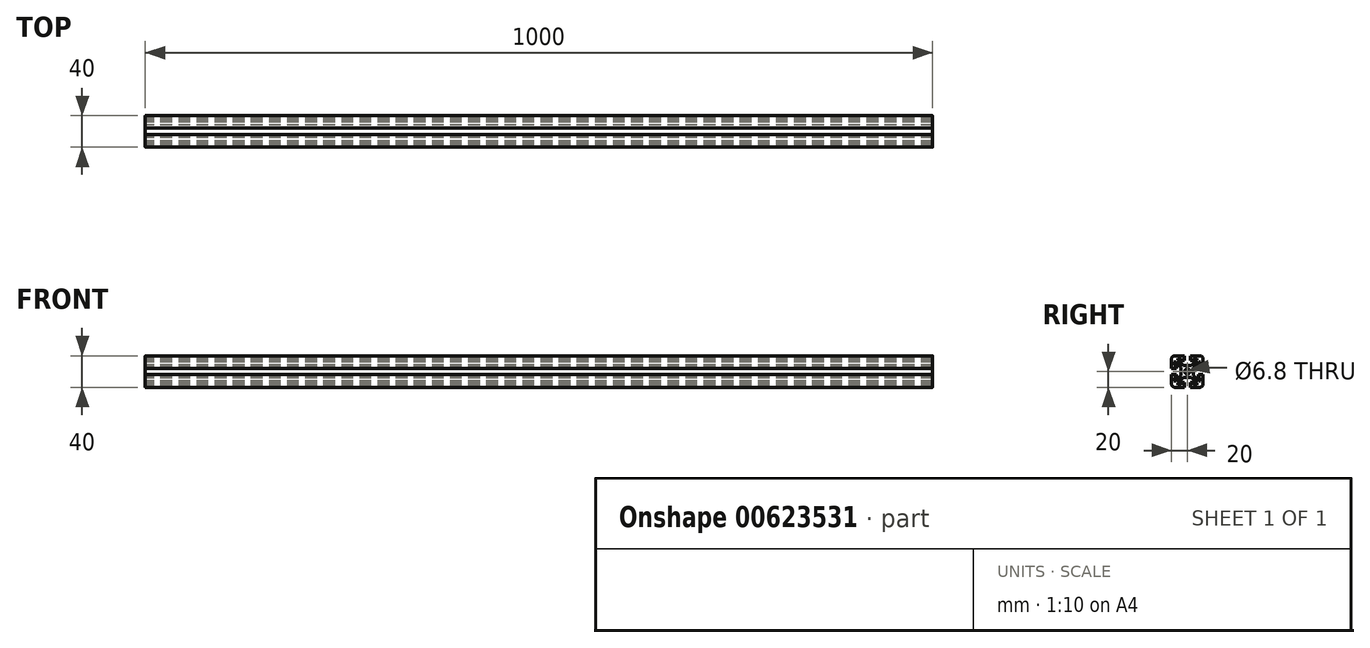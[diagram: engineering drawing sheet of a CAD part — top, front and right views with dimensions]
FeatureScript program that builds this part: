
annotation { "Feature Type Name" : "Feature", "Feature Type Description" : "" }
export const myFeature = defineFeature(function(context is Context, id is Id, definition is map)
    precondition{}
    {
        {
            var Q0;
            Q0=qCreatedBy(makeId("Right.planeOp"),FACE);
            var sketch = newSketch(context, id + "F0", { "sketchPlane" : qUnion([Q0])});
            skLineSegment(sketch, "E0", {"start": v(-5, 7.8) * mm, "end": v(5, 7.8) * mm});
            skLineSegment(sketch, "E1", {"start": v(5, 7.8) * mm, "end": v(12, 14.8) * mm});
            skLineSegment(sketch, "E2", {"start": v(12, 14.8) * mm, "end": v(12, 16.83) * mm});
            skLineSegment(sketch, "E3", {"start": v(12, 16.83) * mm, "end": v(8, 16.83) * mm});
            skLineSegment(sketch, "E4", {"start": v(8, 16.83) * mm, "end": v(8, 13.83) * mm});
            skLineSegment(sketch, "E5", {"start": v(8, 13.83) * mm, "end": v(4, 13.83) * mm});
            skLineSegment(sketch, "E6", {"start": v(4, 13.83) * mm, "end": v(4, 20) * mm});
            skLineSegment(sketch, "E7", {"start": v(4, 20) * mm, "end": v(16, 20) * mm});
            skLineSegment(sketch, "E8.MirrorCS", {"start": v(-5, 7.8) * mm, "end": v(-12, 14.8) * mm});
            skLineSegment(sketch, "E9.MirrorCS", {"start": v(-4, 13.83) * mm, "end": v(-4, 20) * mm});
            skLineSegment(sketch, "E10.MirrorCS", {"start": v(-12, 14.8) * mm, "end": v(-12, 16.83) * mm});
            skLineSegment(sketch, "E11.MirrorCS", {"start": v(-8, 16.83) * mm, "end": v(-8, 13.83) * mm});
            skLineSegment(sketch, "E12.MirrorCS", {"start": v(-12, 16.83) * mm, "end": v(-8, 16.83) * mm});
            skLineSegment(sketch, "E13.MirrorCS", {"start": v(-8, 13.83) * mm, "end": v(-4, 13.83) * mm});
            skPoint(sketch, "E14.visualSharp", {"position": v(20, 20) * mm});
            skArc(sketch, "E14.filletArc", {"start": v(20, 16) * mm, "mid": v(18.83, 18.83) * mm, "end": v(16, 20) * mm});
            skLineSegment(sketch, "E15.MirrorCS", {"start": v(-4, 20) * mm, "end": v(-16, 20) * mm});
            skPoint(sketch, "E16.MirrorP", {"position": v(-20, 20) * mm});
            skLineSegment(sketch, "E17.1.0", {"start": v(-7.8, -5) * mm, "end": v(-14.8, -12) * mm});
            skLineSegment(sketch, "E17.1.1", {"start": v(-16.83, 12) * mm, "end": v(-16.83, 8) * mm});
            skLineSegment(sketch, "E17.1.3", {"start": v(-20, 4) * mm, "end": v(-20, 16) * mm});
            skLineSegment(sketch, "E17.1.4", {"start": v(-14.8, 12) * mm, "end": v(-16.83, 12) * mm});
            skLineSegment(sketch, "E17.1.5", {"start": v(-7.8, -5) * mm, "end": v(-7.8, 5) * mm});
            skLineSegment(sketch, "E17.1.6", {"start": v(-16.83, 8) * mm, "end": v(-13.83, 8) * mm});
            skLineSegment(sketch, "E17.1.7", {"start": v(-13.83, -4) * mm, "end": v(-20, -4) * mm});
            skLineSegment(sketch, "E17.1.8", {"start": v(-14.8, -12) * mm, "end": v(-16.83, -12) * mm});
            skLineSegment(sketch, "E17.1.9", {"start": v(-16.83, -8) * mm, "end": v(-13.83, -8) * mm});
            skLineSegment(sketch, "E17.1.10", {"start": v(-20, -4) * mm, "end": v(-20, -16) * mm});
            skLineSegment(sketch, "E17.1.11", {"start": v(-7.8, 5) * mm, "end": v(-14.8, 12) * mm});
            skLineSegment(sketch, "E17.1.12", {"start": v(-13.83, -8) * mm, "end": v(-13.83, -4) * mm});
            skLineSegment(sketch, "E17.1.13", {"start": v(-13.83, 4) * mm, "end": v(-20, 4) * mm});
            skLineSegment(sketch, "E17.1.14", {"start": v(-16.83, -12) * mm, "end": v(-16.83, -8) * mm});
            skLineSegment(sketch, "E17.1.15", {"start": v(-13.83, 8) * mm, "end": v(-13.83, 4) * mm});
            skArc(sketch, "E17.1.16", {"start": v(-16, 20) * mm, "mid": v(-18.83, 18.83) * mm, "end": v(-20, 16) * mm});
            skLineSegment(sketch, "E17.2.0", {"start": v(5, -7.8) * mm, "end": v(12, -14.8) * mm});
            skLineSegment(sketch, "E17.2.1", {"start": v(-12, -16.83) * mm, "end": v(-8, -16.83) * mm});
            skPoint(sketch, "E17.2.2", {"position": v(-20, -20) * mm});
            skLineSegment(sketch, "E17.2.3", {"start": v(-4, -20) * mm, "end": v(-16, -20) * mm});
            skLineSegment(sketch, "E17.2.4", {"start": v(-12, -14.8) * mm, "end": v(-12, -16.83) * mm});
            skLineSegment(sketch, "E17.2.5", {"start": v(5, -7.8) * mm, "end": v(-5, -7.8) * mm});
            skLineSegment(sketch, "E17.2.6", {"start": v(-8, -16.83) * mm, "end": v(-8, -13.83) * mm});
            skLineSegment(sketch, "E17.2.7", {"start": v(4, -13.83) * mm, "end": v(4, -20) * mm});
            skLineSegment(sketch, "E17.2.8", {"start": v(12, -14.8) * mm, "end": v(12, -16.83) * mm});
            skLineSegment(sketch, "E17.2.9", {"start": v(8, -16.83) * mm, "end": v(8, -13.83) * mm});
            skLineSegment(sketch, "E17.2.10", {"start": v(4, -20) * mm, "end": v(16, -20) * mm});
            skLineSegment(sketch, "E17.2.11", {"start": v(-5, -7.8) * mm, "end": v(-12, -14.8) * mm});
            skLineSegment(sketch, "E17.2.12", {"start": v(8, -13.83) * mm, "end": v(4, -13.83) * mm});
            skLineSegment(sketch, "E17.2.13", {"start": v(-4, -13.83) * mm, "end": v(-4, -20) * mm});
            skLineSegment(sketch, "E17.2.14", {"start": v(12, -16.83) * mm, "end": v(8, -16.83) * mm});
            skLineSegment(sketch, "E17.2.15", {"start": v(-8, -13.83) * mm, "end": v(-4, -13.83) * mm});
            skArc(sketch, "E17.2.16", {"start": v(-20, -16) * mm, "mid": v(-18.83, -18.83) * mm, "end": v(-16, -20) * mm});
            skLineSegment(sketch, "E17.3.0", {"start": v(7.8, 5) * mm, "end": v(14.8, 12) * mm});
            skLineSegment(sketch, "E17.3.1", {"start": v(16.83, -12) * mm, "end": v(16.83, -8) * mm});
            skPoint(sketch, "E17.3.2", {"position": v(20, -20) * mm});
            skLineSegment(sketch, "E17.3.3", {"start": v(20, -4) * mm, "end": v(20, -16) * mm});
            skLineSegment(sketch, "E17.3.4", {"start": v(14.8, -12) * mm, "end": v(16.83, -12) * mm});
            skLineSegment(sketch, "E17.3.5", {"start": v(7.8, 5) * mm, "end": v(7.8, -5) * mm});
            skLineSegment(sketch, "E17.3.6", {"start": v(16.83, -8) * mm, "end": v(13.83, -8) * mm});
            skLineSegment(sketch, "E17.3.7", {"start": v(13.83, 4) * mm, "end": v(20, 4) * mm});
            skLineSegment(sketch, "E17.3.8", {"start": v(14.8, 12) * mm, "end": v(16.83, 12) * mm});
            skLineSegment(sketch, "E17.3.9", {"start": v(16.83, 8) * mm, "end": v(13.83, 8) * mm});
            skLineSegment(sketch, "E17.3.10", {"start": v(20, 4) * mm, "end": v(20, 16) * mm});
            skLineSegment(sketch, "E17.3.11", {"start": v(7.8, -5) * mm, "end": v(14.8, -12) * mm});
            skLineSegment(sketch, "E17.3.12", {"start": v(13.83, 8) * mm, "end": v(13.83, 4) * mm});
            skLineSegment(sketch, "E17.3.13", {"start": v(13.83, -4) * mm, "end": v(20, -4) * mm});
            skLineSegment(sketch, "E17.3.14", {"start": v(16.83, 12) * mm, "end": v(16.83, 8) * mm});
            skLineSegment(sketch, "E17.3.15", {"start": v(13.83, -8) * mm, "end": v(13.83, -4) * mm});
            skArc(sketch, "E17.3.16", {"start": v(16, -20) * mm, "mid": v(18.83, -18.83) * mm, "end": v(20, -16) * mm});
            skPoint(sketch, "E17.center", {"position": v(0, 0) * mm});
            skCircle(sketch, "E18", {"center": v(0, 0) * mm, "radius": 3.4 * mm});
            skSolve(sketch);
        }
        {
            var Q0;
            Q0 = qSketchRegion(id + "F0", true);
            extrude(context, id + "F1", {"entities" : qUnion([Q0]), "depth" : 1000 * mm, "offsetDistance" : 25 * mm});
        }
    });
